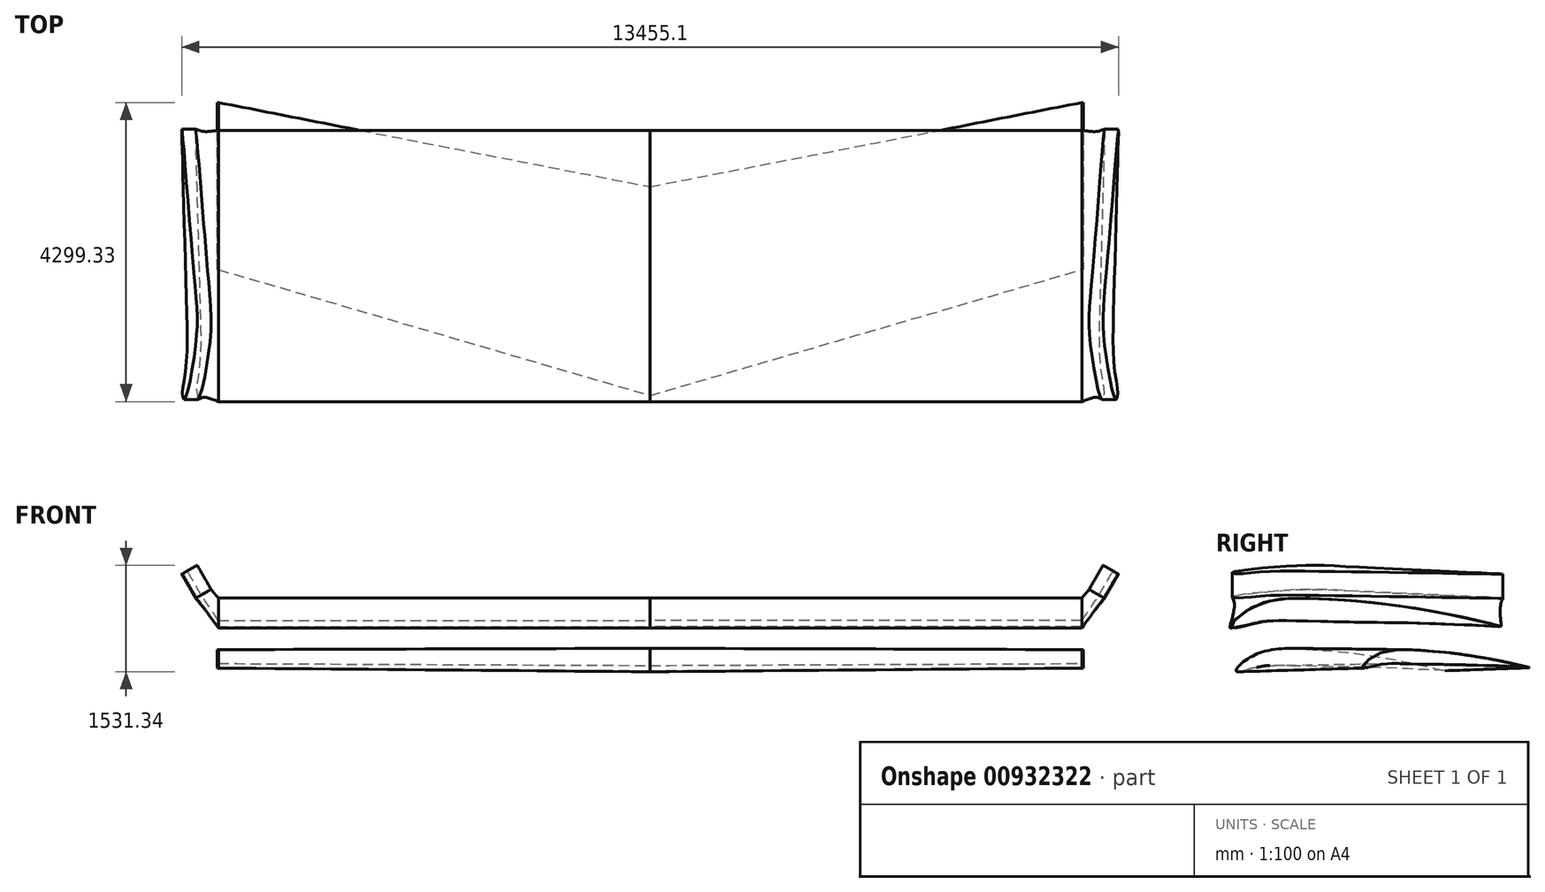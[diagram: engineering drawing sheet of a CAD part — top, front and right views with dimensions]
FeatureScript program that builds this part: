
annotation { "Feature Type Name" : "Feature", "Feature Type Description" : "" }
export const myFeature = defineFeature(function(context is Context, id is Id, definition is map)
    precondition{}
    {
        {
            var Q0;
            Q0=qCreatedBy(makeId("Right.planeOp"),FACE);
            var sketch = newSketch(context, id + "F0", { "sketchPlane" : qUnion([Q0])});
            skFitSpline(sketch, "E0", {"points": [v(-1100.92, -157.2) * mm, v(-1061.48, -79.7) * mm, v(-898.45, 42.48) * mm, v(-685.63, 131.36) * mm, v(-370.93, 171.25) * mm, v(-203.86, 164.63) * mm, v(136.09, 142.74) * mm, v(316.54, 130.5) * mm, v(572.82, 101.38) * mm, v(1077.47, 25.06) * mm, v(1541.63, -67.54) * mm, v(1759.08, -118.01) * mm, v(1813.44, -131.6) * mm, v(1899.03, -150.92) * mm, v(1783.12, -143.1) * mm, v(1674.79, -138.23) * mm, v(974.7, -106.37) * mm, v(277.71, -92.77) * mm, v(-126.12, -83.07) * mm, v(-370.93, -80.17) * mm, v(-528, -76.93) * mm, v(-677.5, -79.18) * mm, v(-823.12, -106.37) * mm, v(-923.39, -129.4) * mm, v(-1042.12, -162.3) * mm, v(-1100.92, -157.2) * mm]});
            skLineSegment(sketch, "E1", {"start": v(-1100.92, -157.2) * mm, "end": v(1899.03, -174.05) * mm, "construction": true});
            skLineSegment(sketch, "E2", {"start": v(-370.93, 54.75) * mm, "end": v(-370.93, 171.25) * mm, "construction": true});
            skLineSegment(sketch, "E3", {"start": v(-370.93, 54.75) * mm, "end": v(-1100.92, 58.85) * mm, "construction": true});
            skSolve(sketch);
        }
        {
            var Q0;
            Q0=qCreatedBy(makeId("Top.planeOp"),FACE);
            var sketch = newSketch(context, id + "F1", { "sketchPlane" : qUnion([Q0])});
            skLineSegment(sketch, "E4", {"start": v(0, 1896.04) * mm, "end": v(0, -1103.96) * mm, "construction": true});
            skLineSegment(sketch, "E5", {"start": v(0, -1103.96) * mm, "end": v(6200, 712.3) * mm, "construction": true});
            skLineSegment(sketch, "E6", {"start": v(6200, 3112.3) * mm, "end": v(0, 1896.04) * mm, "construction": true});
            skLineSegment(sketch, "E7", {"start": v(0, -353.96) * mm, "end": v(6200, -353.96) * mm, "construction": true});
            skLineSegment(sketch, "E8", {"start": v(0, -353.96) * mm, "end": v(0, -1103.96) * mm, "construction": true});
            skLineSegment(sketch, "E9", {"start": v(0, -353.96) * mm, "end": v(6200, 1312.3) * mm, "construction": true});
            skLineSegment(sketch, "E10", {"start": v(6200, 1312.3) * mm, "end": v(6200, 712.3) * mm, "construction": true});
            skLineSegment(sketch, "E11", {"start": v(6200, 3112.3) * mm, "end": v(6200, 1312.3) * mm, "construction": true});
            skSolve(sketch);
        }
        {
            var Q0;
            Q0=sQuery(id+"F1.wireOp",VERTEX,"E9.end");
            var Q1;
            Q1=qCreatedBy(makeId("Right.planeOp"),FACE);
            cPlane(context, id + "F2", {"entities" : qUnion([Q0, Q1]), "cplaneType" : CPlaneType.PLANE_POINT, "offset" : 25 * mm, "width" : 150 * mm, "height" : 150 * mm});
        }
        {
            var Q0;
            Q0=qCreatedBy(id+"F2.planeOp",FACE);
            var sketch = newSketch(context, id + "F3", { "sketchPlane" : qUnion([Q0])});
            skFitSpline(sketch, "E12", {"points": [v(707.32, -100.81) * mm, v(733.87, -48.04) * mm, v(890.62, 66.8) * mm, v(1050.48, 125.79) * mm, v(1291.32, 151.83) * mm, v(1573.57, 140.47) * mm, v(1888.57, 113.25) * mm, v(2063.57, 94.77) * mm, v(2277.46, 62.7) * mm, v(2421.34, 39.36) * mm, v(2593.62, 9.54) * mm, v(2750.64, -22.35) * mm, v(2838.96, -41.98) * mm, v(3107.32, -106.34) * mm, v(3005.39, -99.55) * mm, v(2936.46, -95.66) * mm, v(2820.93, -86.93) * mm, v(2040.8, -63.82) * mm, v(1708.76, -58.51) * mm, v(1291.32, -50.28) * mm, v(1221.02, -47.28) * mm, v(1117.23, -47.28) * mm, v(966.81, -59.3) * mm, v(823.89, -91.5) * mm, v(745.22, -112.58) * mm, v(707.32, -100.81) * mm]});
            skLineSegment(sketch, "E13", {"start": v(1291.32, 58.63) * mm, "end": v(1291.32, 151.83) * mm, "construction": true});
            skLineSegment(sketch, "E14", {"start": v(707.32, -194.82) * mm, "end": v(3107.32, -194.82) * mm, "construction": true});
            skLineSegment(sketch, "E15", {"start": v(1291.32, 58.63) * mm, "end": v(707.32, 58.63) * mm, "construction": true});
            skSolve(sketch);
        }
        {
            var Q0;
            Q0=makeQuery(id+"F0.imprint","IMPRINT",FACE,{"disambiguationData":[TD([[makeQuery(id+"F0.imprint","IMPRINT",EDGE,{"derivedFrom":sQuery(id+"F0.wireOp",EDGE,"E0")}),-1.0]])]});
            var Q1;
            Q1=makeQuery(id+"F3.imprint","IMPRINT",FACE,{"disambiguationData":[TD([[makeQuery(id+"F3.imprint","IMPRINT",EDGE,{"derivedFrom":sQuery(id+"F3.wireOp",EDGE,"E12")}),-1.0]])]});
            loft(context, id + "F4", {"sheetProfilesArray" : [{ "sheetProfileEntities" : qUnion([Q0]) }, { "sheetProfileEntities" : qUnion([Q1]) }]});
        }
        {
            var Q0;
            Q0=makeQuery(id+"F3.imprint","IMPRINT",FACE,{"disambiguationData":[TD([[makeQuery(id+"F3.imprint","IMPRINT",EDGE,{"derivedFrom":sQuery(id+"F3.wireOp",EDGE,"E12")}),-1.0]])]});
            extrude(context, id + "F5", {"entities" : qUnion([Q0]), "operationType" : NewBodyOperationType.ADD, "depth" : 20 * mm, "offsetDistance" : 25 * mm});
        }
        {
            var Q0;
            Q0=makeQuery(id+"F4.opLoft","SWEPT_BODY",BODY,{"disambiguationData":[OSD([makeQuery(id+"F0.imprint","IMPRINT",FACE,{"disambiguationData":[TD([[makeQuery(id+"F0.imprint","IMPRINT",EDGE,{"derivedFrom":sQuery(id+"F0.wireOp",EDGE,"E0")}),-1.0]])]}),makeQuery(id+"F3.imprint","IMPRINT",FACE,{"disambiguationData":[TD([[makeQuery(id+"F3.imprint","IMPRINT",EDGE,{"derivedFrom":sQuery(id+"F3.wireOp",EDGE,"E12")}),-1.0]])]})])]});
            var Q1;
            Q1=qCreatedBy(makeId("Right.planeOp"),FACE);
            mirror(context, id + "F6", {"entities" : qUnion([Q0]), "mirrorPlane" : qUnion([Q1])});
        }
        {
            var Q0;
            Q0=qCreatedBy(makeId("Right.planeOp"),FACE);
            var sketch = newSketch(context, id + "F7", { "sketchPlane" : qUnion([Q0])});
            skLineSegment(sketch, "E16", {"start": v(-1281.04, 1202.5) * mm, "end": v(2718.96, 1202.5) * mm, "construction": true});
            skFitSpline(sketch, "E17", {"points": [v(-1171.88, 461.12) * mm, v(-1189.61, 468.71) * mm, v(-1187.08, 500.37) * mm, v(-1147.83, 554.81) * mm, v(-1002.21, 680.17) * mm, v(-835.08, 777.66) * mm, v(-662.88, 842.24) * mm, v(-509.67, 875.16) * mm, v(-333.67, 890.35) * mm, v(-209.58, 892.89) * mm, v(0.6, 887.82) * mm, v(337.41, 871.36) * mm, v(623.57, 851.1) * mm, v(1004.7, 810.58) * mm, v(1414.94, 754.87) * mm, v(1932.8, 663.7) * mm, v(2434.22, 556.08) * mm, v(2667.2, 497.84) * mm, v(2707.71, 485.17) * mm, v(2616.55, 485.17) * mm, v(2379.77, 499.1) * mm, v(1754.27, 526.96) * mm, v(1222.48, 539.62) * mm, v(757.79, 544.68) * mm, v(390.6, 552.28) * mm, v(60.12, 559.88) * mm, v(-257.7, 564.94) * mm, v(-419.77, 570) * mm, v(-541.32, 567.48) * mm, v(-676.8, 559.88) * mm, v(-824.95, 534.55) * mm, v(-999.68, 488.97) * mm, v(-1138.96, 461.12) * mm, v(-1171.88, 461.12) * mm]});
            skSolve(sketch);
        }
        {
            var Q0;
            Q0=makeQuery(id+"F7.imprint","IMPRINT",FACE,{"disambiguationData":[TD([[makeQuery(id+"F7.imprint","IMPRINT",EDGE,{"derivedFrom":sQuery(id+"F7.wireOp",EDGE,"E17")}),-1.0]])]});
            extrude(context, id + "F8", {"entities" : qUnion([Q0]), "depth" : 6200 * mm, "offsetDistance" : 25 * mm});
        }
        {
            var Q0;
            Q0=qCreatedBy(makeId("Front.planeOp"),FACE);
            var sketch = newSketch(context, id + "F9", { "sketchPlane" : qUnion([Q0])});
            skLineSegment(sketch, "E18", {"start": v(6197.58, 619.44) * mm, "end": v(6597.58, 619.44) * mm, "construction": true});
            skLineSegment(sketch, "E19", {"start": v(6597.58, 619.44) * mm, "end": v(6597.58, 1312.26) * mm, "construction": true});
            skLineSegment(sketch, "E20", {"start": v(6197.58, 619.44) * mm, "end": v(6597.58, 1312.26) * mm});
            skLineSegment(sketch, "E21", {"start": v(6597.58, 1312.26) * mm, "end": v(7105.2, 2191.5) * mm});
            skSolve(sketch);
        }
        {
            var Q0;
            Q0=sQuery(id+"F9.wireOp",EDGE,"E20");
            var Q1;
            Q1=sQuery(id+"F9.wireOp",VERTEX,"E19.end");
            cPlane(context, id + "F10", {"entities" : qUnion([Q0, Q1]), "cplaneType" : CPlaneType.LINE_POINT, "offset" : 25 * mm, "width" : 150 * mm, "height" : 150 * mm});
        }
        {
            var Q0;
            Q0=sQuery(id+"F9.wireOp",EDGE,"E20");
            cPoint(context, id + "F11", {"entities" : qUnion([Q0]), "parameter" : 0.5});
        }
        {
            var Q0;
            Q0 = qCreatedBy(id + "F11" ,VERTEX);
            var Q1;
            Q1=sQuery(id+"F9.wireOp",EDGE,"E20");
            cPlane(context, id + "F12", {"entities" : qUnion([Q0, Q1]), "cplaneType" : CPlaneType.LINE_POINT, "offset" : 25 * mm, "width" : 150 * mm, "height" : 150 * mm});
        }
        {
            var Q0;
            Q0=qCreatedBy(id+"F12.planeOp",FACE);
            var sketch = newSketch(context, id + "F13", { "sketchPlane" : qUnion([Q0])});
            skFitSpline(sketch, "E22", {"points": [v(5164.58, -1159.36) * mm, v(4973.8, -359.28) * mm, v(5008.17, 679.95) * mm, v(5205.45, 2726.23) * mm, v(5205.62, 2619.5) * mm, v(5181.53, 1879.53) * mm, v(5127.73, 170.64) * mm, v(5133.6, -659.48) * mm, v(5196.14, -1033.77) * mm, v(5192.97, -1117.25) * mm, v(5164.58, -1159.36) * mm]});
            skSolve(sketch);
        }
        {
            var Q1;
            Q1=makeQuery(id+"F13.imprint","IMPRINT",FACE,{"disambiguationData":[TD([[makeQuery(id+"F13.imprint","IMPRINT",EDGE,{"derivedFrom":sQuery(id+"F13.wireOp",EDGE,"E22")}),-1.0]])]});
            var Q2;
            Q2=makeQuery(id+"F8.opExtrude","CAP_FACE",FACE,{"disambiguationData":[OSD([sQuery(id+"F7.wireOp",EDGE,"E17")])],"isStart":false});
            loft(context, id + "F14", {"operationType" : NewBodyOperationType.ADD, "sheetProfilesArray" : [{ "sheetProfileEntities" : qUnion([Q1]) }, { "sheetProfileEntities" : qUnion([Q2]) }]});
        }
        {
            var Q0;
            Q0=makeQuery(id+"F14.opLoft","CAP_FACE",FACE,{"disambiguationData":[OSD([makeQuery(id+"F13.imprint","IMPRINT",FACE,{"disambiguationData":[TD([[makeQuery(id+"F13.imprint","IMPRINT",EDGE,{"derivedFrom":sQuery(id+"F13.wireOp",EDGE,"E22")}),-1.0]])]})])],"isStart":true});
            extrude(context, id + "F15", {"entities" : qUnion([Q0]), "operationType" : NewBodyOperationType.ADD, "depth" : 400 * mm, "offsetDistance" : 25 * mm});
        }
        {
            var Q0;
            Q0=sQuery(id+"F9.wireOp",EDGE,"E21");
            var Q1;
            Q1=sQuery(id+"F9.wireOp",VERTEX,"E21.end");
            cPlane(context, id + "F16", {"entities" : qUnion([Q0, Q1]), "cplaneType" : CPlaneType.LINE_POINT, "offset" : 25 * mm, "width" : 150 * mm, "height" : 150 * mm});
        }
        {
            var Q0;
            Q0=makeQuery(id+"F8.opExtrude","SWEPT_BODY",BODY,{"disambiguationData":[OSD([sQuery(id+"F7.wireOp",EDGE,"E17")])]});
            var Q1;
            Q1=qCreatedBy(makeId("Right.planeOp"),FACE);
            mirror(context, id + "F17", {"entities" : qUnion([Q0]), "mirrorPlane" : qUnion([Q1])});
        }
    });
